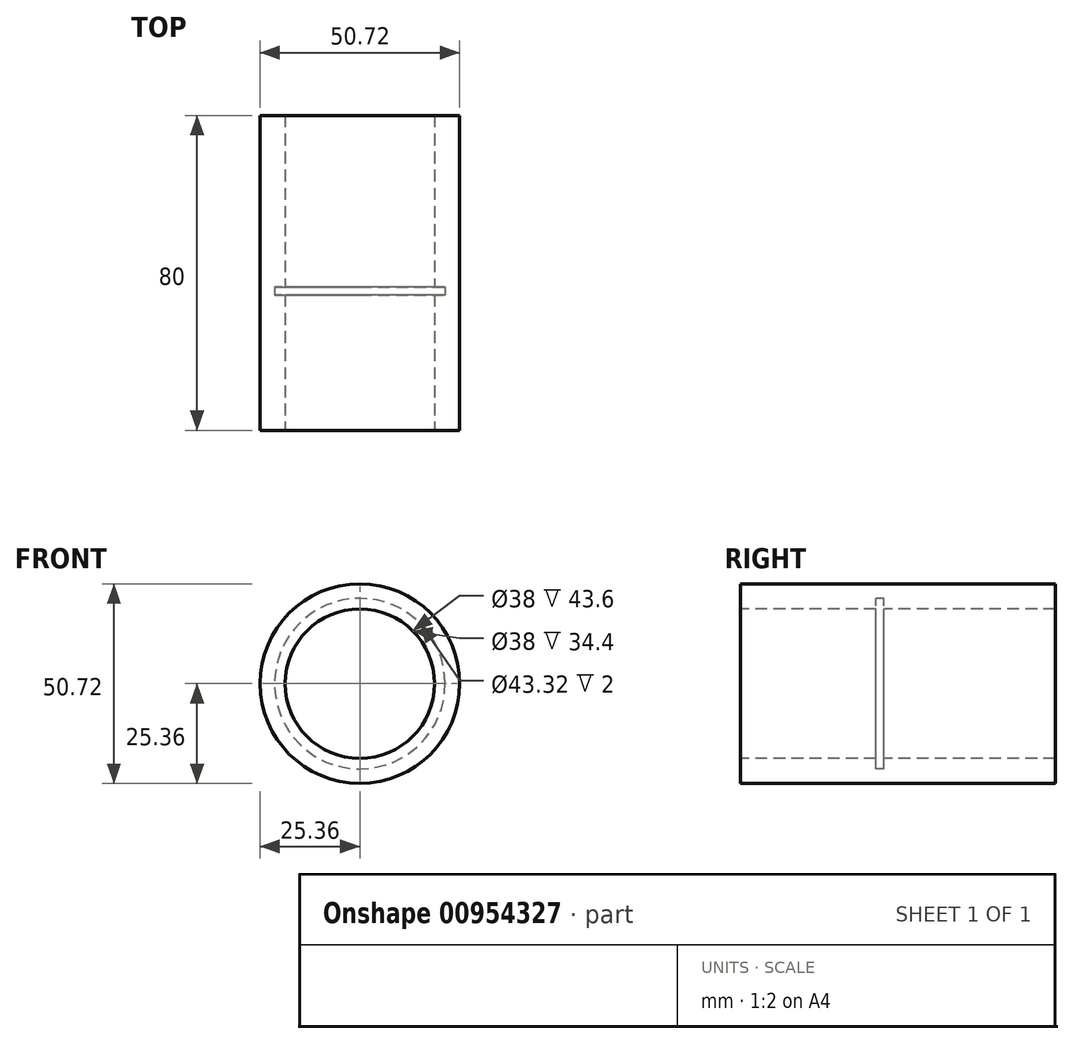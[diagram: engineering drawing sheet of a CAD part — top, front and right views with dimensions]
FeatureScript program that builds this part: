
annotation { "Feature Type Name" : "Feature", "Feature Type Description" : "" }
export const myFeature = defineFeature(function(context is Context, id is Id, definition is map)
    precondition{}
    {
        {
            var Q0;
            Q0=qCreatedBy(makeId("Front.planeOp"),FACE);
            var sketch = newSketch(context, id + "F0", { "sketchPlane" : qUnion([Q0])});
            skCircle(sketch, "E0", {"center": v(0, 0) * mm, "radius": 25.36 * mm});
            skSolve(sketch);
        }
        {
            var Q0;
            Q0=makeQuery(id+"F0.imprint","IMPRINT",FACE,{"disambiguationData":[TD([[makeQuery(id+"F0.imprint","IMPRINT",EDGE,{"derivedFrom":sQuery(id+"F0.wireOp",EDGE,"E0")}),1.0]])]});
            extrude(context, id + "F1", {"entities" : qUnion([Q0]), "oppositeDirection" : true, "depth" : 80 * mm, "offsetDistance" : 25 * mm});
        }
        {
            var Q0;
            Q0=makeQuery(id+"F1.opExtrude","CAP_FACE",FACE,{"disambiguationData":[OSD([sQuery(id+"F0.wireOp",EDGE,"E0")])],"isStart":true});
            var sketch = newSketch(context, id + "F2", { "sketchPlane" : qUnion([Q0])});
            skCircle(sketch, "E1", {"center": v(0, 0) * mm, "radius": 19 * mm});
            skSolve(sketch);
        }
        {
            var Q0;
            Q0=makeQuery(id+"F2.imprint","IMPRINT",FACE,{"disambiguationData":[TD([[makeQuery(id+"F2.imprint","IMPRINT",EDGE,{"derivedFrom":sQuery(id+"F2.wireOp",EDGE,"E1")}),1.0]])]});
            var Q1;
            Q1=sQuery(id+"F2.wireOp",EDGE,"E1");
            extrude(context, id + "F3", {"entities" : qUnion([Q0]), "operationType" : NewBodyOperationType.REMOVE, "surfaceEntities" : qUnion([Q1]), "oppositeDirection" : true, "depth" : 99.8 * mm, "offsetDistance" : 25 * mm});
        }
        {
            var Q0;
            Q0=qCreatedBy(makeId("Front.planeOp"),FACE);
            cPlane(context, id + "F4", {"entities" : qUnion([Q0]), "cplaneType" : CPlaneType.OFFSET, "offset" : 34.4 * mm, "oppositeDirection" : true, "width" : 150 * mm, "height" : 150 * mm});
        }
        {
            var Q0;
            Q0=qCreatedBy(id+"F4.planeOp",FACE);
            var sketch = newSketch(context, id + "F5", { "sketchPlane" : qUnion([Q0])});
            skCircle(sketch, "E2", {"center": v(0, 0) * mm, "radius": 21.66 * mm});
            skSolve(sketch);
        }
        {
            var Q0;
            Q0 = qSketchRegion(id + "F5", true);
            extrude(context, id + "F6", {"entities" : qUnion([Q0]), "operationType" : NewBodyOperationType.REMOVE, "oppositeDirection" : true, "depth" : 2 * mm, "offsetDistance" : 25 * mm});
        }
    });
